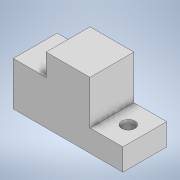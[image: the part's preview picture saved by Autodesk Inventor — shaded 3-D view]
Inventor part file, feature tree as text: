
AUTODESK INVENTOR PART (.ipt)
format: ipt  version: 2022 (Build 260153000, 153)  size: 109,056 bytes
history: native  units: mm
features: extrude x2, sketch x2, other x1
ambient origin geometry x8: Origin, YZ Plane, XZ Plane, XY Plane, X Axis, Y Axis, Z Axis, Center Point
bodies: Body1 (feature_tree)
feature tree (5):
  other  "Sólido1"
  extrude  "Extrusão1"  Depth=10.0mm
  extrude  "Extrusão2"  Depth=15.0mm
  sketch  "Esboço1"  dims[d0=50.0mm d1=10.0mm]
  sketch  "Esboço2"  dims[d2=20.0mm d3=15.0mm d5=20.0mm d7=30.0mm d8=20.0mm d9=0.0mm d10=6.0mm d11=7.5mm d12=10.0mm d13=0.0mm d14=0.0mm]
